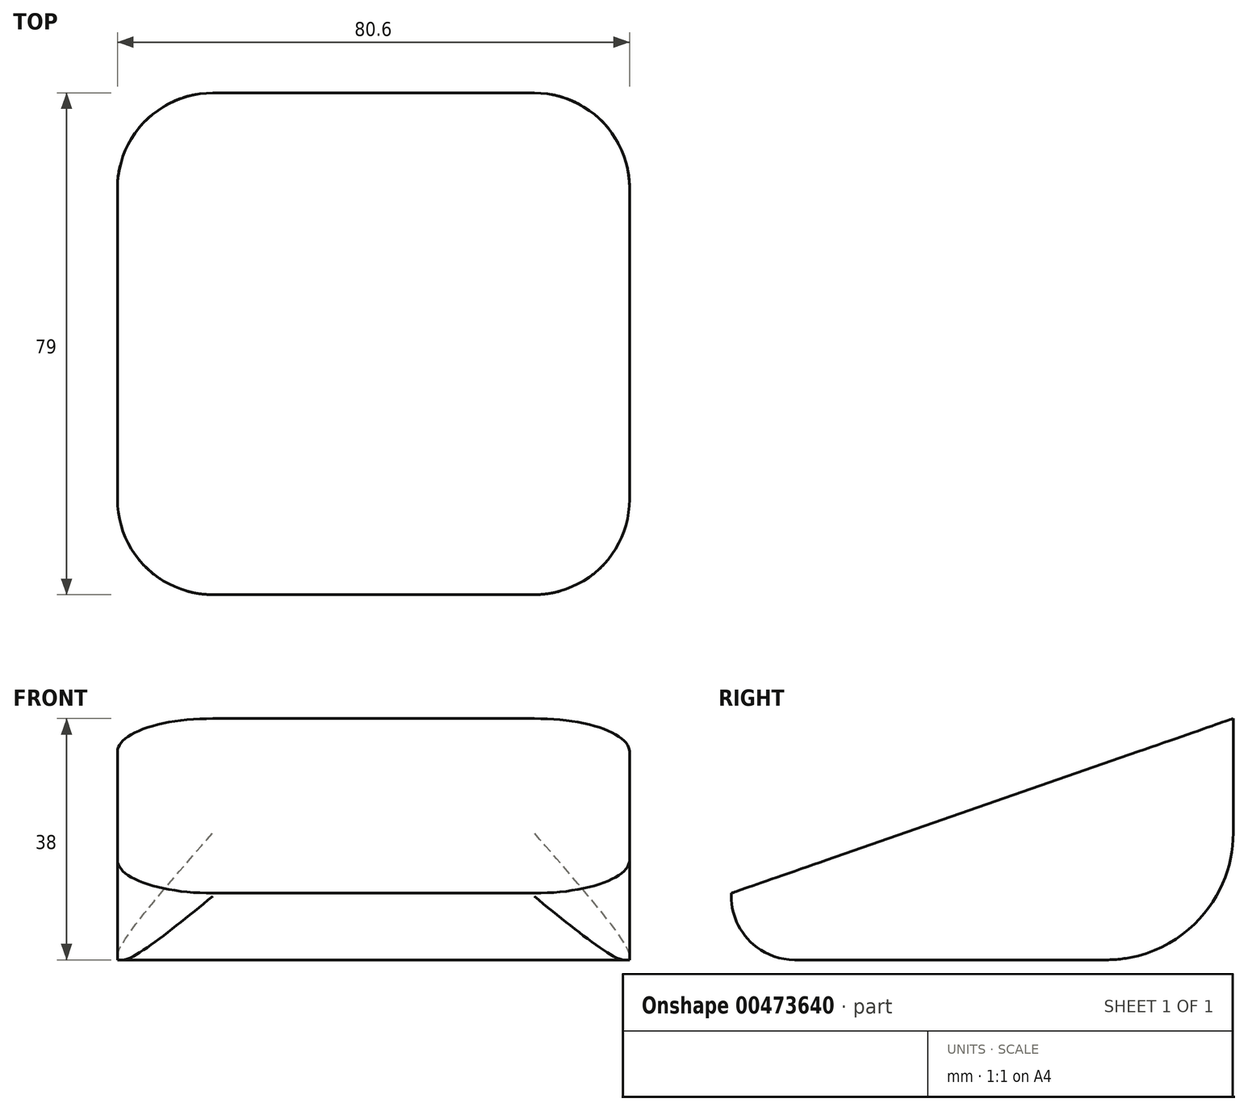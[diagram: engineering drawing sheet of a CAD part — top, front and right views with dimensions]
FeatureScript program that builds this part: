
annotation { "Feature Type Name" : "Feature", "Feature Type Description" : "" }
export const myFeature = defineFeature(function(context is Context, id is Id, definition is map)
    precondition{}
    {
        {
            var Q0;
            Q0=qCreatedBy(makeId("Right.planeOp"),FACE);
            var sketch = newSketch(context, id + "F0", { "sketchPlane" : qUnion([Q0])});
            skLineSegment(sketch, "E0", {"start": v(-39.5, 0) * mm, "end": v(39.5, 0) * mm});
            skLineSegment(sketch, "E1", {"start": v(39.5, 0) * mm, "end": v(39.5, 38) * mm});
            skLineSegment(sketch, "E2", {"start": v(39.5, 38) * mm, "end": v(-39.5, 10.5) * mm});
            skLineSegment(sketch, "E3", {"start": v(-39.5, 10.5) * mm, "end": v(-39.5, 0) * mm});
            skLineSegment(sketch, "E4", {"start": v(0, 0) * mm, "end": v(0, 18.48) * mm, "construction": true});
            skSolve(sketch);
        }
        {
            var Q0;
            Q0 = qSketchRegion(id + "F0", true);
            extrude(context, id + "F1", {"entities" : qUnion([Q0]), "endBound" : BoundingType.SYMMETRIC, "depth" : 80.6 * mm});
        }
        {
            var Q0;
            Q0=makeQuery(id+"F1.opExtrude","CAP_EDGE",EDGE,{"disambiguationData":[OSD([sQuery(id+"F0.wireOp",EDGE,"E3")])],"isStart":false});
            var Q1;
            Q1=makeQuery(id+"F1.opExtrude","CAP_EDGE",EDGE,{"disambiguationData":[OSD([sQuery(id+"F0.wireOp",EDGE,"E1")])],"isStart":false});
            var Q2;
            Q2=makeQuery(id+"F1.opExtrude","CAP_EDGE",EDGE,{"disambiguationData":[OSD([sQuery(id+"F0.wireOp",EDGE,"E3")])],"isStart":true});
            var Q3;
            Q3=makeQuery(id+"F1.opExtrude","CAP_EDGE",EDGE,{"disambiguationData":[OSD([sQuery(id+"F0.wireOp",EDGE,"E1")])],"isStart":true});
            fillet(context, id + "F2", {"entities" : qUnion([Q0, Q1, Q2, Q3]), "radius" : 15 * mm, "tangentPropagation" : true, "allowEdgeOverflow" : false});
        }
        {
            var Q0;
            Q0=makeQuery(id+"F1.opExtrude","SWEPT_EDGE",EDGE,{"disambiguationData":[OSD([sQuery(id+"F0.wireOp",EDGE,"E0"),sQuery(id+"F0.wireOp",EDGE,"E1")])]});
            fillet(context, id + "F3", {"entities" : qUnion([Q0]), "radius" : 20 * mm, "allowEdgeOverflow" : false});
        }
        {
            var Q0;
            Q0=makeQuery(id+"F1.opExtrude","SWEPT_EDGE",EDGE,{"disambiguationData":[OSD([sQuery(id+"F0.wireOp",EDGE,"E0"),sQuery(id+"F0.wireOp",EDGE,"E3")])]});
            fillet(context, id + "F4", {"entities" : qUnion([Q0]), "radius" : 10 * mm, "allowEdgeOverflow" : false});
        }
    });
